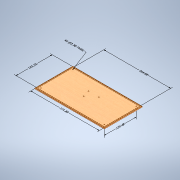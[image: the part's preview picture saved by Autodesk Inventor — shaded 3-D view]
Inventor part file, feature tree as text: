
AUTODESK INVENTOR PART (.ipt)
format: ipt  version: 2022 (Build 260153000, 153)  size: 194,560 bytes
history: native  units: mm
features: other x5, extrude x5, sketch x5, mirror x2, hole x1
ambient origin geometry x8: Origin, YZ Plane, XZ Plane, XY Plane, X Axis, Y Axis, Z Axis, Center Point
bodies: Solid1 (feature_tree)
feature tree (18):
  other  "Annotations"
  extrude  "Bottom_Base"  Depth=3.572mm
  extrude  "Side_Insert"  Depth=1.5875mm
  mirror  "Mirrored_Side_Insert"
  extrude  "Front_Insert"  Depth=3.572mm
  mirror  "Back_Insert"
  extrude  "Joint_Holes"  Depth=0.8mm TaperAngle=0.0deg
  extrude  "Makey_Makey_Mounting_Holes"  Depth=271.825mm
  sketch  "Sketch1"  dims[d2=0.0mm d3=3.572mm]
  sketch  "Sketch2"  dims[d4=1.5875mm d5=1.5875mm]
  sketch  "Sketch3"  dims[d6=0.8mm d7=0.0mm d8=3.572mm]
  sketch  "Sketch4"  dims[d9=1.5875mm d10=0.8mm d11=0.0mm]
  sketch  "Sketch5"  dims[d18=3.3mm d19=6.6mm d20=6.6mm d21=6.6mm d22=6.6mm d23=0.0mm d24=0.0mm d27=275.0mm d32=126.481mm d34=94.0mm d35=48.0mm d36=3.3mm d37=3.5mm d38=26.4mm d39=26.4mm d40=33.3mm d41=27.3mm d42=10.0mm d43=0.0mm d12=0.167694mm d13=0.260382mm d14=143.253mm d15=8.279997mm d16=0.523652mm d17=264.681mm d25=55.304283mm d28=8.303899mm d29=0.853148mm d30=271.825mm d33=126.481mm]
  other  "Linear Dimension 1"
  other  "Linear Dimension 2"
  hole  "Hole Note 1"  [1 undecoded]
  other  "Linear Dimension 3"
  other  "Linear Dimension 4"
note: 1 required parameter value undecoded (feature->parameter linkage not recoverable at this tier; creation-order binding heuristic only, values carry confidence <= 0.55)
